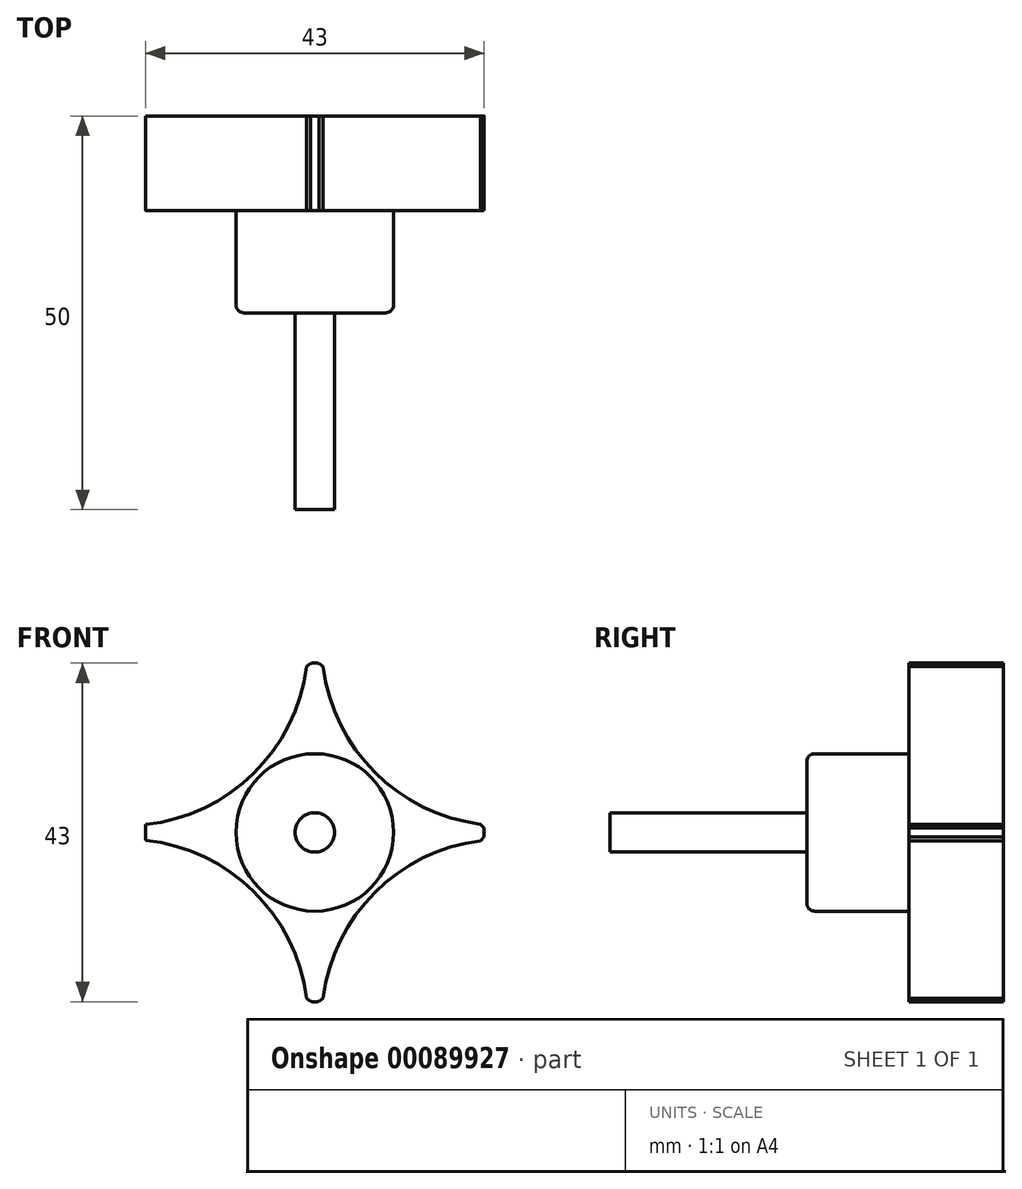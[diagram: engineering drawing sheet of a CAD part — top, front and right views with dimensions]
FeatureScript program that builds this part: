
annotation { "Feature Type Name" : "Feature", "Feature Type Description" : "" }
export const myFeature = defineFeature(function(context is Context, id is Id, definition is map)
    precondition{}
    {
        {
            var Q0;
            Q0=qCreatedBy(makeId("Front.planeOp"),FACE);
            var sketch = newSketch(context, id + "F0", { "sketchPlane" : qUnion([Q0])});
            skCircle(sketch, "E0", {"center": v(0, 0) * mm, "radius": 21.5 * mm});
            skSolve(sketch);
        }
        {
            var Q0;
            Q0=makeQuery(id+"F0.imprint","IMPRINT",FACE,{"disambiguationData":[TD([[makeQuery(id+"F0.imprint","IMPRINT",EDGE,{"derivedFrom":sQuery(id+"F0.wireOp",EDGE,"E0")}),1.0]])]});
            extrude(context, id + "F1", {"entities" : qUnion([Q0]), "depth" : 12 * mm});
        }
        {
            var Q0;
            Q0=makeQuery(id+"F1.opExtrude","CAP_FACE",FACE,{"disambiguationData":[OSD([sQuery(id+"F0.wireOp",EDGE,"E0")])],"isStart":false});
            var sketch = newSketch(context, id + "F2", { "sketchPlane" : qUnion([Q0])});
            skLineSegment(sketch, "E1", {"start": v(0, 35) * mm, "end": v(-1, 35) * mm});
            skArc(sketch, "E2", {"start": v(-21.48, 1) * mm, "mid": v(-7.63, 7.63) * mm, "end": v(-1, 21.48) * mm});
            skPoint(sketch, "E3.end.orphan", {"position": v(-1, 0) * mm});
            skPoint(sketch, "E4.end.orphan", {"position": v(0, 1) * mm});
            skPoint(sketch, "E5.center.orphan", {"position": v(0, 0) * mm});
            skLineSegment(sketch, "E6", {"start": v(-1, 0) * mm, "end": v(0, 0) * mm});
            skLineSegment(sketch, "E7", {"start": v(0, 0) * mm, "end": v(-1, 0) * mm});
            skLineSegment(sketch, "E8", {"start": v(0, 0) * mm, "end": v(0, 1) * mm});
            skArc(sketch, "E9", {"start": v(-1, 21.48) * mm, "mid": v(-15.2, 15.2) * mm, "end": v(-21.48, 1) * mm});
            skLineSegment(sketch, "E10.trimOffspring", {"start": v(0, 1) * mm, "end": v(0, 0) * mm});
            skLineSegment(sketch, "E11.trimOffspring", {"start": v(0, 1) * mm, "end": v(0, 0) * mm, "construction": true});
            skPoint(sketch, "E12.start.orphan", {"position": v(-21.48, 0) * mm});
            skPoint(sketch, "E13.orphan", {"position": v(0, 21.5) * mm});
            skLineSegment(sketch, "E14", {"start": v(0, 0) * mm, "end": v(0, 27.93) * mm});
            skLineSegment(sketch, "E15", {"start": v(0, 0) * mm, "end": v(0, 27.93) * mm, "construction": true});
            skArc(sketch, "E16.MirrorCS", {"start": v(21.48, 1) * mm, "mid": v(7.63, 7.63) * mm, "end": v(1, 21.48) * mm});
            skArc(sketch, "E17.MirrorCS", {"start": v(1, 21.48) * mm, "mid": v(15.2, 15.2) * mm, "end": v(21.48, 1) * mm});
            skArc(sketch, "E18.MirrorCS", {"start": v(-21.48, -1) * mm, "mid": v(-7.63, -7.63) * mm, "end": v(-1, -21.48) * mm});
            skArc(sketch, "E19.MirrorCS", {"start": v(-1, -21.48) * mm, "mid": v(-15.2, -15.2) * mm, "end": v(-21.48, -1) * mm});
            skArc(sketch, "E20.MirrorCS", {"start": v(21.48, -1) * mm, "mid": v(7.63, -7.63) * mm, "end": v(1, -21.48) * mm});
            skArc(sketch, "E21.MirrorCS", {"start": v(1, -21.48) * mm, "mid": v(15.2, -15.2) * mm, "end": v(21.48, -1) * mm});
            skSolve(sketch);
        }
        {
            var Q0;
            Q0 = qSketchRegion(id + "F2", true);
            extrude(context, id + "F3", {"entities" : qUnion([Q0]), "operationType" : NewBodyOperationType.REMOVE, "oppositeDirection" : true, "depth" : 12 * mm});
        }
        {
            var Q0;
            Q0=makeQuery(id+"F1.opExtrude","CAP_FACE",FACE,{"disambiguationData":[OSD([sQuery(id+"F0.wireOp",EDGE,"E0")])],"isStart":false});
            var sketch = newSketch(context, id + "F4", { "sketchPlane" : qUnion([Q0])});
            skCircle(sketch, "E22", {"center": v(0, 0) * mm, "radius": 10 * mm});
            skSolve(sketch);
        }
        {
            var Q0;
            Q0 = qSketchRegion(id + "F4", true);
            extrude(context, id + "F5", {"entities" : qUnion([Q0]), "operationType" : NewBodyOperationType.ADD, "depth" : 13 * mm});
        }
        {
            var Q0;
            Q0=makeQuery(id+"F5.opExtrude","CAP_FACE",FACE,{"disambiguationData":[OSD([sQuery(id+"F4.wireOp",EDGE,"E22")])],"isStart":false});
            var sketch = newSketch(context, id + "F6", { "sketchPlane" : qUnion([Q0])});
            skCircle(sketch, "E23", {"center": v(0, 0) * mm, "radius": 2.5 * mm});
            skSolve(sketch);
        }
        {
            var Q0;
            Q0 = qSketchRegion(id + "F6", true);
            extrude(context, id + "F7", {"entities" : qUnion([Q0]), "operationType" : NewBodyOperationType.ADD, "depth" : 25 * mm});
        }
        {
            var Q0;
            {var subQ0=sQuery(id+"F2.wireOp",EDGE,"E9");var subQ1=sQuery(id+"F2.wireOp",EDGE,"E2");var subQ2=sQuery(id+"F0.wireOp",EDGE,"E0");Q0=makeQuery(id+"F3.boolean.opBoolean","COPY",EDGE,{"derivedFrom":makeQuery(id+"F3.opExtrude","SWEPT_EDGE",EDGE,{"disambiguationData":[OSD([subQ2,subQ1,subQ0]),TDD([makeQuery(id+"F2.imprint","INTERSECT",VERTEX,{"disambiguationData":[OD(0.0)],"derivedFrom":[makeQuery(id+"F1.opExtrude","CAP_EDGE",EDGE,{"disambiguationData":[OSD([subQ2])],"isStart":false}),subQ1,subQ0]})])]})});}
            var Q1;
            {var subQ0=sQuery(id+"F2.wireOp",EDGE,"E9");var subQ1=sQuery(id+"F2.wireOp",EDGE,"E2");var subQ2=sQuery(id+"F0.wireOp",EDGE,"E0");Q1=makeQuery(id+"F3.boolean.opBoolean","COPY",EDGE,{"derivedFrom":makeQuery(id+"F3.opExtrude","SWEPT_EDGE",EDGE,{"disambiguationData":[OSD([subQ2,subQ1,subQ0]),TDD([makeQuery(id+"F2.imprint","INTERSECT",VERTEX,{"disambiguationData":[OD(1.0)],"derivedFrom":[makeQuery(id+"F1.opExtrude","CAP_EDGE",EDGE,{"disambiguationData":[OSD([subQ2])],"isStart":false}),subQ1,subQ0]})])]})});}
            var Q2;
            {var subQ0=sQuery(id+"F2.wireOp",EDGE,"E19.MirrorCS");var subQ1=sQuery(id+"F2.wireOp",EDGE,"E18.MirrorCS");var subQ2=sQuery(id+"F0.wireOp",EDGE,"E0");Q2=makeQuery(id+"F3.boolean.opBoolean","COPY",EDGE,{"derivedFrom":makeQuery(id+"F3.opExtrude","SWEPT_EDGE",EDGE,{"disambiguationData":[OSD([subQ2,subQ1,subQ0]),TDD([makeQuery(id+"F2.imprint","INTERSECT",VERTEX,{"disambiguationData":[OD(0.0)],"derivedFrom":[makeQuery(id+"F1.opExtrude","CAP_EDGE",EDGE,{"disambiguationData":[OSD([subQ2])],"isStart":false}),subQ1,subQ0]})])]})});}
            var Q3;
            {var subQ0=sQuery(id+"F2.wireOp",EDGE,"E17.MirrorCS");var subQ1=sQuery(id+"F2.wireOp",EDGE,"E16.MirrorCS");var subQ2=sQuery(id+"F0.wireOp",EDGE,"E0");Q3=makeQuery(id+"F3.boolean.opBoolean","COPY",EDGE,{"derivedFrom":makeQuery(id+"F3.opExtrude","SWEPT_EDGE",EDGE,{"disambiguationData":[OSD([subQ2,subQ1,subQ0]),TDD([makeQuery(id+"F2.imprint","INTERSECT",VERTEX,{"disambiguationData":[OD(1.0)],"derivedFrom":[makeQuery(id+"F1.opExtrude","CAP_EDGE",EDGE,{"disambiguationData":[OSD([subQ2])],"isStart":false}),subQ1,subQ0]})])]})});}
            var Q4;
            {var subQ0=sQuery(id+"F2.wireOp",EDGE,"E17.MirrorCS");var subQ1=sQuery(id+"F2.wireOp",EDGE,"E16.MirrorCS");var subQ2=sQuery(id+"F0.wireOp",EDGE,"E0");Q4=makeQuery(id+"F3.boolean.opBoolean","COPY",EDGE,{"derivedFrom":makeQuery(id+"F3.opExtrude","SWEPT_EDGE",EDGE,{"disambiguationData":[OSD([subQ2,subQ1,subQ0]),TDD([makeQuery(id+"F2.imprint","INTERSECT",VERTEX,{"disambiguationData":[OD(0.0)],"derivedFrom":[makeQuery(id+"F1.opExtrude","CAP_EDGE",EDGE,{"disambiguationData":[OSD([subQ2])],"isStart":false}),subQ1,subQ0]})])]})});}
            var Q5;
            {var subQ0=sQuery(id+"F2.wireOp",EDGE,"E21.MirrorCS");var subQ1=sQuery(id+"F2.wireOp",EDGE,"E20.MirrorCS");var subQ2=sQuery(id+"F0.wireOp",EDGE,"E0");Q5=makeQuery(id+"F3.boolean.opBoolean","COPY",EDGE,{"derivedFrom":makeQuery(id+"F3.opExtrude","SWEPT_EDGE",EDGE,{"disambiguationData":[OSD([subQ2,subQ1,subQ0]),TDD([makeQuery(id+"F2.imprint","INTERSECT",VERTEX,{"disambiguationData":[OD(0.0)],"derivedFrom":[makeQuery(id+"F1.opExtrude","CAP_EDGE",EDGE,{"disambiguationData":[OSD([subQ2])],"isStart":false}),subQ1,subQ0]})])]})});}
            var Q6;
            {var subQ0=sQuery(id+"F2.wireOp",EDGE,"E19.MirrorCS");var subQ1=sQuery(id+"F2.wireOp",EDGE,"E18.MirrorCS");var subQ2=sQuery(id+"F0.wireOp",EDGE,"E0");Q6=makeQuery(id+"F3.boolean.opBoolean","COPY",EDGE,{"derivedFrom":makeQuery(id+"F3.opExtrude","SWEPT_EDGE",EDGE,{"disambiguationData":[OSD([subQ2,subQ1,subQ0]),TDD([makeQuery(id+"F2.imprint","INTERSECT",VERTEX,{"disambiguationData":[OD(1.0)],"derivedFrom":[makeQuery(id+"F1.opExtrude","CAP_EDGE",EDGE,{"disambiguationData":[OSD([subQ2])],"isStart":false}),subQ1,subQ0]})])]})});}
            var Q7;
            {var subQ0=sQuery(id+"F2.wireOp",EDGE,"E21.MirrorCS");var subQ1=sQuery(id+"F2.wireOp",EDGE,"E20.MirrorCS");var subQ2=sQuery(id+"F0.wireOp",EDGE,"E0");Q7=makeQuery(id+"F3.boolean.opBoolean","COPY",EDGE,{"derivedFrom":makeQuery(id+"F3.opExtrude","SWEPT_EDGE",EDGE,{"disambiguationData":[OSD([subQ2,subQ1,subQ0]),TDD([makeQuery(id+"F2.imprint","INTERSECT",VERTEX,{"disambiguationData":[OD(1.0)],"derivedFrom":[makeQuery(id+"F1.opExtrude","CAP_EDGE",EDGE,{"disambiguationData":[OSD([subQ2])],"isStart":false}),subQ1,subQ0]})])]})});}
            chamfer(context, id + "F8", {"entities" : qUnion([Q0, Q1, Q2, Q3, Q4, Q5, Q6, Q7]), "width" : .5 * mm, "tangentPropagation" : true});
        }
        {
            var Q0;
            Q0=makeQuery(id+"F5.opExtrude","CAP_EDGE",EDGE,{"disambiguationData":[OSD([sQuery(id+"F4.wireOp",EDGE,"E22")])],"isStart":false});
            fillet(context, id + "F9", {"entities" : qUnion([Q0]), "radius" : 1 * mm, "tangentPropagation" : true, "allowEdgeOverflow" : false});
        }
    });
